# Revit family: HBG7 UFO
name_source: partatom
category: Lighting Fixtures
units: mm (PartAtom-declared; Revit-internal decimal feet)

## family parameters
Always vertical = Yes
Cut with Voids When Loaded = Yes
Light Source = Yes
Maintain Annotation Orientation = No
OmniClass Number = 23.80.70.00
OmniClass Title = Lighting
Part Type = Normal
Room Calculation Point = No
Round Connector Dimension = Use Diameter
Shared = No
Work Plane-Based = No

## types (3) — shared parameters
CRI = 80
Color Filter = 16777215
Default Elevation = 0' - 0"
Dimming Lamp Color Temperature Shift = <None>
IP Rating = 65
Input Voltage = 120-277V/347-480V
Lamp = LED
Load Classification = Lighting
Manufacturer = Above All Lighting
Power Factor = 0.9
Tilt Angle = 90.00°
URL = https://www.abovealllighting.com

## per-type parameters (varying)
| type | Model | Photometric Web File | Wattage Comments |
| HBG7-150SP-3000K-90D | HBG7-150SP-SW1-HK-90-BK | HBG7-150W-90D.IES | 150W |
| HBG7-240SP-3000K-90D | HBG7-240SP-SW1-HK-90-BK | HBG7-240W-90D.IES | 240W |
| HBG7-150SP-3000K-110D | HBG7-150SP-SW1-HK-110-BK | HBG7-150W-110D-3000K.IES | 150W |

## geometry (parser evidence)
native form markers: Sweep x2
no freeform markers — native parametric forms only
